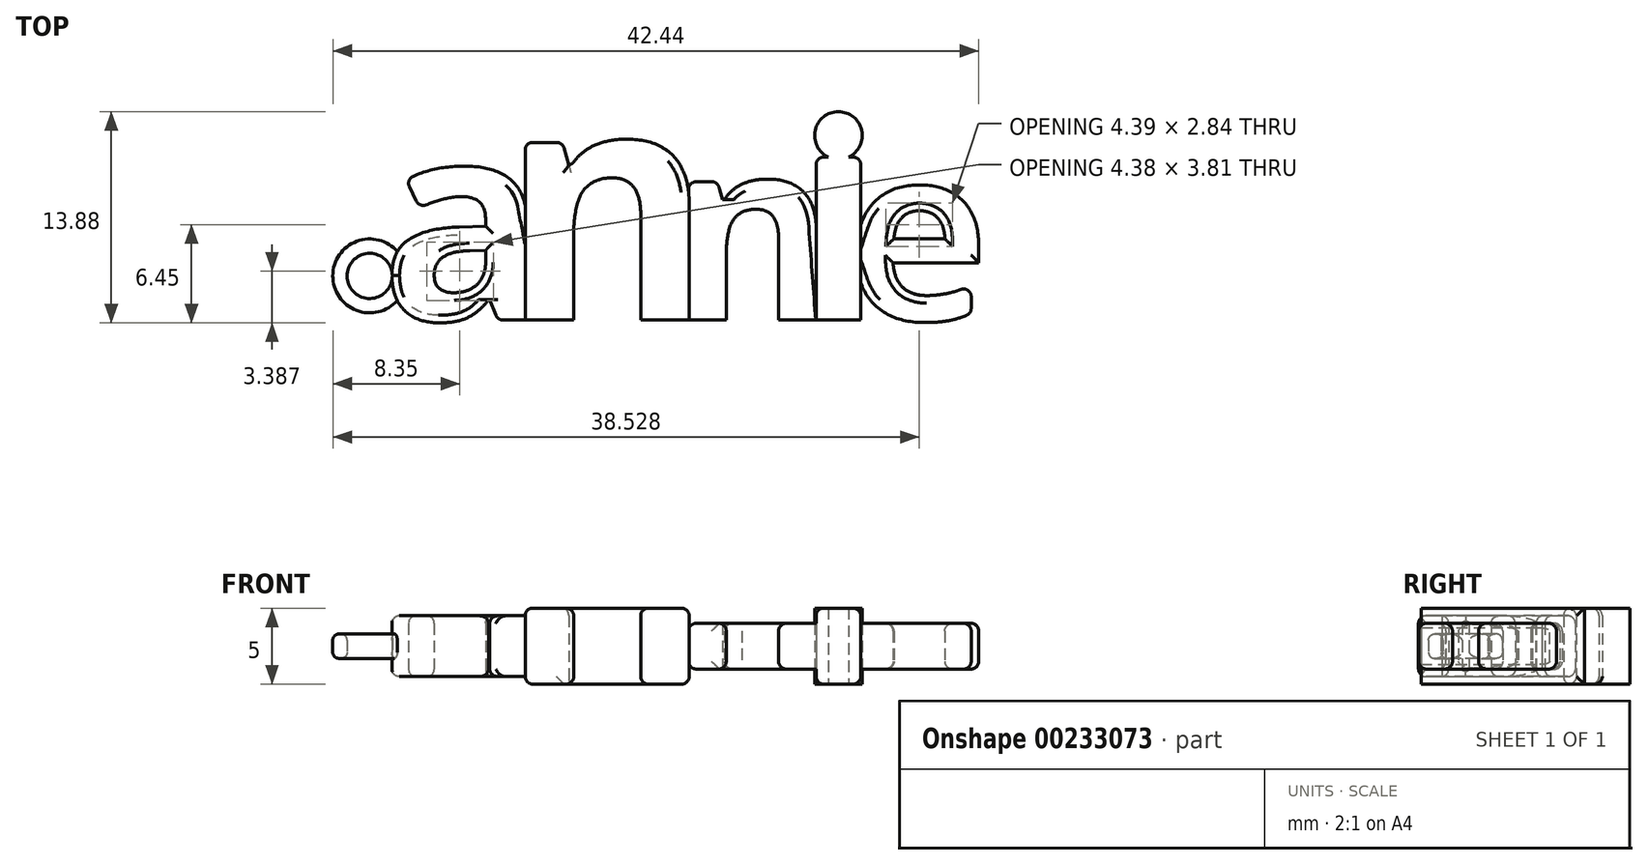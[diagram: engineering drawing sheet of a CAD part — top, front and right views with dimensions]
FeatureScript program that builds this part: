
annotation { "Feature Type Name" : "Feature", "Feature Type Description" : "" }
export const myFeature = defineFeature(function(context is Context, id is Id, definition is map)
    precondition{}
    {
        {
            var Q0;
            Q0=qCreatedBy(makeId("Top.planeOp"),FACE);
            var sketch = newSketch(context, id + "F0", { "sketchPlane" : qUnion([Q0])});
            skText(sketch, "E0", { "text": "a", "fontName": "OpenSans-Bold.ttf"});
            skText(sketch, "E1", { "text": "n", "fontName": "OpenSans-Bold.ttf"});
            skText(sketch, "E2", { "text": "n", "fontName": "OpenSans-Bold.ttf"});
            skText(sketch, "E3", { "text": "e", "fontName": "OpenSans-Bold.ttf"});
            skLineSegment(sketch, "E4.bottom", {"start": v(4.28, 10.72) * mm, "end": v(7.22, 10.72) * mm});
            skLineSegment(sketch, "E4.top", {"start": v(4.28, 0) * mm, "end": v(7.22, 0) * mm});
            skLineSegment(sketch, "E4.left", {"start": v(4.28, 10.72) * mm, "end": v(4.28, 0) * mm});
            skLineSegment(sketch, "E4.right", {"start": v(7.22, 10.72) * mm, "end": v(7.22, 0) * mm});
            skCircle(sketch, "E5", {"center": v(-25.05, 2.9) * mm, "radius": 2.43 * mm});
            skCircle(sketch, "E6", {"center": v(-25.05, 2.9) * mm, "radius": 1.48 * mm});
            skCircle(sketch, "E7", {"center": v(5.75, 12.13) * mm, "radius": 1.57 * mm});
            skPoint(sketch, "E7.centerSnap0", {"position": v(5.75, 10.72) * mm});
            const initialGuessF0  = {"E0": [-0.02435, 0, 1, 0, 0.01308], "E1": [-0.0165, 0, 1, 0, 0.0154], "E2": [-0.0054, 0, 1, 0, 0.012], "E3": [0.00622, 0, 1, 0, 0.0115]};
            skSetInitialGuess(sketch, initialGuessF0);
            skSolve(sketch);
        }
        {
            var Q0;
            {var subQ0=sQuery(id+"F0.wireOp",EDGE,"E5");var subQ1=sQuery(id+"F0.wireOp",EDGE,"E0.sketch_text.stroke-5");var subQ2=makeQuery(id+"F0.imprint","INTERSECT",VERTEX,{"derivedFrom":[subQ1,subQ0]});Q0=makeQuery(id+"F0.imprint","IMPRINT",FACE,{"disambiguationData":[TD([[makeQuery(id+"F0.imprint","IMPRINT",EDGE,{"disambiguationData":[TD([[subQ2,-1.0]])],"derivedFrom":subQ1}),-1.0]])]});}
            var Q1;
            Q1=makeQuery(id+"F0.imprint","IMPRINT",FACE,{"disambiguationData":[TD([[makeQuery(id+"F0.imprint","IMPRINT",EDGE,{"derivedFrom":sQuery(id+"F0.wireOp",EDGE,"E0.sketch_text.stroke-0")}),-1.0]])]});
            extrude(context, id + "F1", {"entities" : qUnion([Q0, Q1]), "depth" : 2 * mm, "hasSecondDirection" : true, "secondDirectionOppositeDirection" : true, "secondDirectionDepth" : 2 * mm});
        }
        {
            var Q0;
            {var subQ2=sQuery(id+"F0.wireOp",EDGE,"E1.sketch_text.stroke-16");Q0=makeQuery(id+"F0.imprint","IMPRINT",FACE,{"disambiguationData":[TD([[makeQuery(id+"F0.imprint","IMPRINT",EDGE,{"derivedFrom":subQ2}),1.0]])]});}
            extrude(context, id + "F2", {"entities" : qUnion([Q0]), "operationType" : NewBodyOperationType.ADD, "depth" : 1.5 * mm, "hasSecondDirection" : true, "secondDirectionOppositeDirection" : true, "secondDirectionDepth" : 1.5 * mm});
        }
        {
            var Q0;
            {var subQ1=sQuery(id+"F0.wireOp",EDGE,"E0.sketch_text.stroke-16");Q0=makeQuery(id+"F0.imprint","IMPRINT",FACE,{"disambiguationData":[TD([[makeQuery(id+"F0.imprint","IMPRINT",EDGE,{"derivedFrom":subQ1}),1.0]])]});}
            var Q1;
            {var subQ0=sQuery(id+"F0.wireOp",EDGE,"E0.sketch_text.stroke-16");Q1=makeQuery(id+"F0.imprint","IMPRINT",FACE,{"disambiguationData":[TD([[makeQuery(id+"F0.imprint","IMPRINT",EDGE,{"derivedFrom":subQ0}),-1.0]])]});}
            var Q2;
            {var subQ0=sQuery(id+"F0.wireOp",EDGE,"E1.sketch_text.stroke-16");Q2=makeQuery(id+"F0.imprint","IMPRINT",FACE,{"disambiguationData":[TD([[makeQuery(id+"F0.imprint","IMPRINT",EDGE,{"derivedFrom":subQ0}),-1.0]])]});}
            extrude(context, id + "F3", {"entities" : qUnion([Q0, Q1, Q2]), "depth" : 2.5 * mm, "hasSecondDirection" : true, "secondDirectionOppositeDirection" : true, "secondDirectionDepth" : 2.5 * mm});
        }
        {
            var Q0;
            {var subQ6=sQuery(id+"F0.wireOp",EDGE,"E2.sketch_text.stroke-16");Q0=makeQuery(id+"F0.imprint","IMPRINT",FACE,{"disambiguationData":[TD([[makeQuery(id+"F0.imprint","IMPRINT",EDGE,{"derivedFrom":subQ6}),1.0]])]});}
            var Q1;
            {var subQ0=sQuery(id+"F0.wireOp",EDGE,"E3.sketch_text.stroke-7");var subQ1=sQuery(id+"F0.wireOp",EDGE,"E3.sketch_text.stroke-6");var subQ2=makeQuery(id+"F0.imprint","INTERSECT",VERTEX,{"derivedFrom":[subQ1,subQ0]});Q1=makeQuery(id+"F0.imprint","IMPRINT",FACE,{"disambiguationData":[TD([[makeQuery(id+"F0.imprint","IMPRINT",EDGE,{"disambiguationData":[TD([[subQ2,1.0]])],"derivedFrom":subQ1}),-1.0]])]});}
            var Q2;
            {var subQ0=sQuery(id+"F0.wireOp",EDGE,"E7");var subQ1=sQuery(id+"F0.wireOp",EDGE,"E4.bottom");var subQ2=makeQuery(id+"F0.imprint","INTERSECT",VERTEX,{"disambiguationData":[OD(0.0)],"derivedFrom":[subQ1,subQ0]});Q2=makeQuery(id+"F0.imprint","IMPRINT",FACE,{"disambiguationData":[TD([[makeQuery(id+"F0.imprint","IMPRINT",EDGE,{"disambiguationData":[TD([[subQ2,-1.0]])],"derivedFrom":subQ1}),-1.0]])]});}
            var Q3;
            {var subQ0=sQuery(id+"F0.wireOp",EDGE,"E2.sketch_text.stroke-16");Q3=makeQuery(id+"F0.imprint","IMPRINT",FACE,{"disambiguationData":[TD([[makeQuery(id+"F0.imprint","IMPRINT",EDGE,{"derivedFrom":subQ0}),-1.0]])]});}
            var Q4;
            {var subQ0=sQuery(id+"F0.wireOp",EDGE,"E7");var subQ1=sQuery(id+"F0.wireOp",EDGE,"E4.bottom");var subQ2=makeQuery(id+"F0.imprint","INTERSECT",VERTEX,{"disambiguationData":[OD(0.0)],"derivedFrom":[subQ1,subQ0]});Q4=makeQuery(id+"F0.imprint","IMPRINT",FACE,{"disambiguationData":[TD([[makeQuery(id+"F0.imprint","IMPRINT",EDGE,{"disambiguationData":[TD([[subQ2,-1.0]])],"derivedFrom":subQ1}),1.0]])]});}
            extrude(context, id + "F4", {"entities" : qUnion([Q0, Q1, Q2, Q3, Q4]), "operationType" : NewBodyOperationType.ADD, "depth" : 2.5 * mm, "hasSecondDirection" : true, "secondDirectionOppositeDirection" : true, "secondDirectionDepth" : 2.5 * mm});
        }
        {
            var Q0;
            Q0=makeQuery(id+"F0.imprint","IMPRINT",FACE,{"disambiguationData":[TD([[makeQuery(id+"F0.imprint","IMPRINT",EDGE,{"derivedFrom":sQuery(id+"F0.wireOp",EDGE,"E3.sketch_text.stroke-0")}),-1.0]])]});
            extrude(context, id + "F5", {"entities" : qUnion([Q0]), "operationType" : NewBodyOperationType.ADD, "depth" : 1.5 * mm, "hasSecondDirection" : true, "secondDirectionOppositeDirection" : true, "secondDirectionDepth" : 1.5 * mm});
        }
        {
            var Q0;
            {var subQ0=sQuery(id+"F0.wireOp",EDGE,"E5");var subQ1=sQuery(id+"F0.wireOp",EDGE,"E0.sketch_text.stroke-5");var subQ2=makeQuery(id+"F0.imprint","INTERSECT",VERTEX,{"derivedFrom":[subQ1,subQ0]});Q0=makeQuery(id+"F0.imprint","IMPRINT",FACE,{"disambiguationData":[TD([[makeQuery(id+"F0.imprint","IMPRINT",EDGE,{"disambiguationData":[TD([[subQ2,-1.0]])],"derivedFrom":subQ1}),1.0]])]});}
            extrude(context, id + "F6", {"entities" : qUnion([Q0]), "depth" : 0.8 * mm, "hasSecondDirection" : true, "secondDirectionOppositeDirection" : true, "secondDirectionDepth" : 0.8 * mm});
        }
        {
            var Q0;
            Q0=makeQuery(id+"F6.opExtrude","CAP_EDGE",EDGE,{"disambiguationData":[OSD([sQuery(id+"F0.wireOp",EDGE,"E5")])],"isStart":false});
            var Q1;
            Q1=makeQuery(id+"F6.opExtrude","CAP_EDGE",EDGE,{"disambiguationData":[OSD([sQuery(id+"F0.wireOp",EDGE,"E5")])],"isStart":true});
            var Q2;
            Q2=makeQuery(id+"F6.opExtrude","CAP_EDGE",EDGE,{"disambiguationData":[OSD([sQuery(id+"F0.wireOp",EDGE,"E6")])],"isStart":false});
            var Q3;
            Q3=makeQuery(id+"F6.opExtrude","CAP_EDGE",EDGE,{"disambiguationData":[OSD([sQuery(id+"F0.wireOp",EDGE,"E6")])],"isStart":true});
            fillet(context, id + "F7", {"entities" : qUnion([Q0, Q1, Q2, Q3]), "radius" : 0.4 * mm, "tangentPropagation" : true, "allowEdgeOverflow" : false});
        }
        {
            var Q0;
            {var subQ0=sQuery(id+"F0.wireOp",EDGE,"E0.sketch_text.stroke-2");var subQ1=sQuery(id+"F0.wireOp",EDGE,"E0.sketch_text.stroke-1");Q0=makeQuery(id+"F1.boolean.opBoolean","MERGE",EDGE,{"derivedFrom":[makeQuery(id+"FrYbtXQuBTiY2Ud_0.opExtrude","SWEPT_EDGE",EDGE,{"disambiguationData":[OSD([subQ1,subQ0])]}),makeQuery(id+"F1.opExtrude","SWEPT_EDGE",EDGE,{"disambiguationData":[OSD([subQ1,subQ0])]})]});}
            var Q1;
            {var subQ0=sQuery(id+"F0.wireOp",EDGE,"E0.sketch_text.stroke-1");var subQ1=sQuery(id+"F0.wireOp",EDGE,"E0.sketch_text.stroke-0");Q1=makeQuery(id+"F1.boolean.opBoolean","MERGE",EDGE,{"derivedFrom":[makeQuery(id+"FrYbtXQuBTiY2Ud_0.opExtrude","SWEPT_EDGE",EDGE,{"disambiguationData":[OSD([subQ1,subQ0])]}),makeQuery(id+"F1.opExtrude","SWEPT_EDGE",EDGE,{"disambiguationData":[OSD([subQ1,subQ0])]})]});}
            var Q2;
            {var subQ0=sQuery(id+"F0.wireOp",EDGE,"E1.sketch_text.stroke-12");var subQ1=sQuery(id+"F0.wireOp",EDGE,"E1.sketch_text.stroke-11");Q2=makeQuery(id+"F3.boolean.opBoolean","MERGE",EDGE,{"derivedFrom":[makeQuery(id+"FrYbtXQuBTiY2Ud_0.opExtrude","SWEPT_EDGE",EDGE,{"disambiguationData":[OSD([subQ1,subQ0])]}),makeQuery(id+"F3.opExtrude","SWEPT_EDGE",EDGE,{"disambiguationData":[OSD([subQ1,subQ0])]})]});}
            var Q3;
            {var subQ0=sQuery(id+"F0.wireOp",EDGE,"E2.sketch_text.stroke-11");var subQ1=sQuery(id+"F0.wireOp",EDGE,"E2.sketch_text.stroke-10");Q3=makeQuery(id+"F2.boolean.opBoolean","MERGE",EDGE,{"derivedFrom":[makeQuery(id+"FrYbtXQuBTiY2Ud_0.opExtrude","SWEPT_EDGE",EDGE,{"disambiguationData":[OSD([subQ1,subQ0])]}),makeQuery(id+"F2.opExtrude","SWEPT_EDGE",EDGE,{"disambiguationData":[OSD([subQ1,subQ0])]})]});}
            var Q4;
            {var subQ0=sQuery(id+"F0.wireOp",EDGE,"E2.sketch_text.stroke-12");var subQ1=sQuery(id+"F0.wireOp",EDGE,"E2.sketch_text.stroke-11");Q4=makeQuery(id+"F2.boolean.opBoolean","MERGE",EDGE,{"derivedFrom":[makeQuery(id+"FrYbtXQuBTiY2Ud_0.opExtrude","SWEPT_EDGE",EDGE,{"disambiguationData":[OSD([subQ1,subQ0])]}),makeQuery(id+"F2.opExtrude","SWEPT_EDGE",EDGE,{"disambiguationData":[OSD([subQ1,subQ0])]})]});}
            fillet(context, id + "F8", {"entities" : qUnion([Q0, Q1, Q2, Q3, Q4]), "radius" : .6 * mm, "tangentPropagation" : true, "allowEdgeOverflow" : false});
        }
        {
            var Q0;
            Q0=makeQuery(id+"F1.opExtrude","CAP_EDGE",EDGE,{"disambiguationData":[OSD([sQuery(id+"F0.wireOp",EDGE,"E0.sketch_text.stroke-14")])],"isStart":false});
            var Q1;
            Q1=makeQuery(id+"F1.opExtrude","CAP_EDGE",EDGE,{"disambiguationData":[OSD([sQuery(id+"F0.wireOp",EDGE,"E0.sketch_text.stroke-15")])],"isStart":false});
            var Q2;
            Q2=makeQuery(id+"F1.opExtrude","CAP_EDGE",EDGE,{"disambiguationData":[OSD([sQuery(id+"F0.wireOp",EDGE,"E0.sketch_text.stroke-0")])],"isStart":false});
            var Q3;
            {var subQ0=sQuery(id+"F0.wireOp",EDGE,"E0.sketch_text.stroke-17");var subQ1=sQuery(id+"F0.wireOp",EDGE,"E0.sketch_text.stroke-0");Q3=makeQuery(id+"F1.boolean.opBoolean","MERGE",EDGE,{"derivedFrom":[makeQuery(id+"FrYbtXQuBTiY2Ud_0.opExtrude","SWEPT_EDGE",EDGE,{"disambiguationData":[OSD([subQ1,subQ0])]}),makeQuery(id+"F1.opExtrude","SWEPT_EDGE",EDGE,{"disambiguationData":[OSD([subQ1,subQ0])]})]});}
            var Q4;
            Q4=makeQuery(id+"F1.opExtrude","CAP_EDGE",EDGE,{"disambiguationData":[OSD([sQuery(id+"F0.wireOp",EDGE,"E0.sketch_text.stroke-2")])],"isStart":false});
            var Q5;
            Q5=makeQuery(id+"F1.opExtrude","CAP_EDGE",EDGE,{"disambiguationData":[OSD([sQuery(id+"F0.wireOp",EDGE,"E0.sketch_text.stroke-8")])],"isStart":false});
            var Q6;
            Q6=makeQuery(id+"F1.opExtrude","CAP_EDGE",EDGE,{"disambiguationData":[OSD([sQuery(id+"F0.wireOp",EDGE,"E0.sketch_text.stroke-11")])],"isStart":false});
            var Q7;
            Q7=makeQuery(id+"F1.opExtrude","CAP_EDGE",EDGE,{"disambiguationData":[OSD([sQuery(id+"F0.wireOp",EDGE,"E0.sketch_text.stroke-12")])],"isStart":false});
            var Q8;
            {var subQ0=sQuery(id+"F0.wireOp",EDGE,"E0.sketch_text.stroke-13");var subQ1=sQuery(id+"F0.wireOp",EDGE,"E0.sketch_text.stroke-12");Q8=makeQuery(id+"F1.boolean.opBoolean","MERGE",EDGE,{"derivedFrom":[makeQuery(id+"FrYbtXQuBTiY2Ud_0.opExtrude","SWEPT_EDGE",EDGE,{"disambiguationData":[OSD([subQ1,subQ0])]}),makeQuery(id+"F1.opExtrude","SWEPT_EDGE",EDGE,{"disambiguationData":[OSD([subQ1,subQ0])]})]});}
            var Q9;
            {var subQ0=sQuery(id+"F0.wireOp",EDGE,"E0.sketch_text.stroke-12");var subQ1=sQuery(id+"F0.wireOp",EDGE,"E0.sketch_text.stroke-11");Q9=makeQuery(id+"F1.boolean.opBoolean","MERGE",EDGE,{"derivedFrom":[makeQuery(id+"FrYbtXQuBTiY2Ud_0.opExtrude","SWEPT_EDGE",EDGE,{"disambiguationData":[OSD([subQ1,subQ0])]}),makeQuery(id+"F1.opExtrude","SWEPT_EDGE",EDGE,{"disambiguationData":[OSD([subQ1,subQ0])]})]});}
            var Q10;
            Q10=makeQuery(id+"F1.opExtrude","CAP_EDGE",EDGE,{"disambiguationData":[OSD([sQuery(id+"F0.wireOp",EDGE,"E0.sketch_text.stroke-12")])],"isStart":true});
            var Q11;
            Q11=makeQuery(id+"F1.opExtrude","CAP_EDGE",EDGE,{"disambiguationData":[OSD([sQuery(id+"F0.wireOp",EDGE,"E0.sketch_text.stroke-7")])],"isStart":false});
            var Q12;
            Q12=makeQuery(id+"F1.opExtrude","CAP_EDGE",EDGE,{"disambiguationData":[OSD([sQuery(id+"F0.wireOp",EDGE,"E0.sketch_text.stroke-21")])],"isStart":false});
            var Q13;
            Q13=makeQuery(id+"F1.opExtrude","CAP_EDGE",EDGE,{"disambiguationData":[OSD([sQuery(id+"F0.wireOp",EDGE,"E0.sketch_text.stroke-22")])],"isStart":false});
            var Q14;
            Q14=makeQuery(id+"F1.opExtrude","CAP_EDGE",EDGE,{"disambiguationData":[OSD([sQuery(id+"F0.wireOp",EDGE,"E0.sketch_text.stroke-23")])],"isStart":false});
            var Q15;
            Q15=makeQuery(id+"F1.opExtrude","CAP_EDGE",EDGE,{"disambiguationData":[OSD([sQuery(id+"F0.wireOp",EDGE,"E0.sketch_text.stroke-24")])],"isStart":false});
            var Q16;
            Q16=makeQuery(id+"F1.opExtrude","CAP_EDGE",EDGE,{"disambiguationData":[OSD([sQuery(id+"F0.wireOp",EDGE,"E0.sketch_text.stroke-18")])],"isStart":false});
            var Q17;
            Q17=makeQuery(id+"F1.opExtrude","CAP_EDGE",EDGE,{"disambiguationData":[OSD([sQuery(id+"F0.wireOp",EDGE,"E0.sketch_text.stroke-0")])],"isStart":true});
            var Q18;
            Q18=makeQuery(id+"F1.opExtrude","CAP_EDGE",EDGE,{"disambiguationData":[OSD([sQuery(id+"F0.wireOp",EDGE,"E0.sketch_text.stroke-2")])],"isStart":true});
            var Q19;
            Q19=makeQuery(id+"F1.opExtrude","CAP_EDGE",EDGE,{"disambiguationData":[OSD([sQuery(id+"F0.wireOp",EDGE,"E0.sketch_text.stroke-18")])],"isStart":true});
            var Q20;
            Q20=makeQuery(id+"F1.opExtrude","CAP_EDGE",EDGE,{"disambiguationData":[OSD([sQuery(id+"F0.wireOp",EDGE,"E0.sketch_text.stroke-24")])],"isStart":true});
            var Q21;
            Q21=makeQuery(id+"F1.opExtrude","CAP_EDGE",EDGE,{"disambiguationData":[OSD([sQuery(id+"F0.wireOp",EDGE,"E0.sketch_text.stroke-23")])],"isStart":true});
            var Q22;
            Q22=makeQuery(id+"F1.opExtrude","CAP_EDGE",EDGE,{"disambiguationData":[OSD([sQuery(id+"F0.wireOp",EDGE,"E0.sketch_text.stroke-22")])],"isStart":true});
            var Q23;
            Q23=makeQuery(id+"F1.opExtrude","CAP_EDGE",EDGE,{"disambiguationData":[OSD([sQuery(id+"F0.wireOp",EDGE,"E0.sketch_text.stroke-21")])],"isStart":true});
            var Q24;
            Q24=makeQuery(id+"F1.opExtrude","CAP_EDGE",EDGE,{"disambiguationData":[OSD([sQuery(id+"F0.wireOp",EDGE,"E0.sketch_text.stroke-7")])],"isStart":true});
            var Q25;
            Q25=makeQuery(id+"F1.opExtrude","CAP_EDGE",EDGE,{"disambiguationData":[OSD([sQuery(id+"F0.wireOp",EDGE,"E0.sketch_text.stroke-8")])],"isStart":true});
            var Q26;
            Q26=makeQuery(id+"F1.opExtrude","CAP_EDGE",EDGE,{"disambiguationData":[OSD([sQuery(id+"F0.wireOp",EDGE,"E0.sketch_text.stroke-11")])],"isStart":true});
            var Q27;
            Q27=makeQuery(id+"F1.opExtrude","CAP_EDGE",EDGE,{"disambiguationData":[OSD([sQuery(id+"F0.wireOp",EDGE,"E0.sketch_text.stroke-14")])],"isStart":true});
            var Q28;
            Q28=makeQuery(id+"F1.opExtrude","CAP_EDGE",EDGE,{"disambiguationData":[OSD([sQuery(id+"F0.wireOp",EDGE,"E0.sketch_text.stroke-15")])],"isStart":true});
            fillet(context, id + "F9", {"entities" : qUnion([Q0, Q1, Q2, Q3, Q4, Q5, Q6, Q7, Q8, Q9, Q10, Q11, Q12, Q13, Q14, Q15, Q16, Q17, Q18, Q19, Q20, Q21, Q22, Q23, Q24, Q25, Q26, Q27, Q28]), "radius" : .5 * mm, "tangentPropagation" : true, "allowEdgeOverflow" : false});
        }
        {
            var Q0;
            Q0=makeQuery(id+"F3.opExtrude","CAP_EDGE",EDGE,{"disambiguationData":[OSD([sQuery(id+"F0.wireOp",EDGE,"E1.sketch_text.stroke-8")])],"isStart":false});
            var Q1;
            Q1=makeQuery(id+"F3.opExtrude","CAP_EDGE",EDGE,{"disambiguationData":[OSD([sQuery(id+"F0.wireOp",EDGE,"E1.sketch_text.stroke-6")])],"isStart":false});
            var Q2;
            Q2=makeQuery(id+"F3.opExtrude","CAP_EDGE",EDGE,{"disambiguationData":[OSD([sQuery(id+"F0.wireOp",EDGE,"E1.sketch_text.stroke-16")])],"isStart":false});
            var Q3;
            Q3=makeQuery(id+"F3.opExtrude","CAP_EDGE",EDGE,{"disambiguationData":[OSD([sQuery(id+"F0.wireOp",EDGE,"E1.sketch_text.stroke-10")])],"isStart":false});
            var Q4;
            Q4=makeQuery(id+"F3.opExtrude","CAP_EDGE",EDGE,{"disambiguationData":[OSD([sQuery(id+"F0.wireOp",EDGE,"E1.sketch_text.stroke-9")])],"isStart":false});
            var Q5;
            {var subQ0=sQuery(id+"F0.wireOp",EDGE,"E1.sketch_text.stroke-9");var subQ1=sQuery(id+"F0.wireOp",EDGE,"E1.sketch_text.stroke-8");Q5=makeQuery(id+"F3.boolean.opBoolean","MERGE",EDGE,{"derivedFrom":[makeQuery(id+"FrYbtXQuBTiY2Ud_0.opExtrude","SWEPT_EDGE",EDGE,{"disambiguationData":[OSD([subQ1,subQ0])]}),makeQuery(id+"F3.opExtrude","SWEPT_EDGE",EDGE,{"disambiguationData":[OSD([subQ1,subQ0])]})]});}
            var Q6;
            Q6=makeQuery(id+"F3.opExtrude","CAP_EDGE",EDGE,{"disambiguationData":[OSD([sQuery(id+"F0.wireOp",EDGE,"E1.sketch_text.stroke-9")])],"isStart":true});
            var Q7;
            {var subQ0=sQuery(id+"F0.wireOp",EDGE,"E1.sketch_text.stroke-10");var subQ1=sQuery(id+"F0.wireOp",EDGE,"E1.sketch_text.stroke-9");Q7=makeQuery(id+"F3.boolean.opBoolean","MERGE",EDGE,{"derivedFrom":[makeQuery(id+"FrYbtXQuBTiY2Ud_0.opExtrude","SWEPT_EDGE",EDGE,{"disambiguationData":[OSD([subQ1,subQ0])]}),makeQuery(id+"F3.opExtrude","SWEPT_EDGE",EDGE,{"disambiguationData":[OSD([subQ1,subQ0])]})]});}
            var Q8;
            Q8=makeQuery(id+"F3.opExtrude","CAP_EDGE",EDGE,{"disambiguationData":[OSD([sQuery(id+"F0.wireOp",EDGE,"E1.sketch_text.stroke-6")])],"isStart":true});
            var Q9;
            Q9=makeQuery(id+"F3.opExtrude","CAP_EDGE",EDGE,{"disambiguationData":[OSD([sQuery(id+"F0.wireOp",EDGE,"E1.sketch_text.stroke-8")])],"isStart":true});
            var Q10;
            Q10=makeQuery(id+"F3.opExtrude","CAP_EDGE",EDGE,{"disambiguationData":[OSD([sQuery(id+"F0.wireOp",EDGE,"E1.sketch_text.stroke-16")])],"isStart":true});
            var Q11;
            {var subQ0=sQuery(id+"F0.wireOp",EDGE,"E2.sketch_text.stroke-9");Q11=makeQuery(id+"F2.boolean.opBoolean","MERGE",FACE,{"derivedFrom":[makeQuery(id+"FrYbtXQuBTiY2Ud_0.opExtrude","SWEPT_FACE",FACE,{"disambiguationData":[OSD([subQ0])]}),makeQuery(id+"F2.opExtrude","SWEPT_FACE",FACE,{"disambiguationData":[OSD([subQ0])]})]});}
            var Q12;
            {var subQ0=sQuery(id+"F0.wireOp",EDGE,"E2.sketch_text.stroke-11");var subQ1=sQuery(id+"F0.wireOp",EDGE,"E2.sketch_text.stroke-10");Q12=makeQuery(id+"F8.opFillet","BLEND_EDGE",EDGE,{"blendedFrom":[makeQuery(id+"F2.boolean.opBoolean","MERGE",EDGE,{"derivedFrom":[makeQuery(id+"FrYbtXQuBTiY2Ud_0.opExtrude","SWEPT_EDGE",EDGE,{"disambiguationData":[OSD([subQ1,subQ0])]}),makeQuery(id+"F2.opExtrude","SWEPT_EDGE",EDGE,{"disambiguationData":[OSD([subQ1,subQ0])]})]}),makeQuery(id+"F2.opExtrude","CAP_FACE",FACE,{"disambiguationData":[OSD([sQuery(id+"F0.wireOp",EDGE,"E1.sketch_text.stroke-15"),sQuery(id+"F0.wireOp",EDGE,"E1.sketch_text.stroke-16"),sQuery(id+"F0.wireOp",EDGE,"E2.sketch_text.stroke-0"),sQuery(id+"F0.wireOp",EDGE,"E2.sketch_text.stroke-1"),sQuery(id+"F0.wireOp",EDGE,"E2.sketch_text.stroke-2"),sQuery(id+"F0.wireOp",EDGE,"E2.sketch_text.stroke-3"),sQuery(id+"F0.wireOp",EDGE,"E2.sketch_text.stroke-4"),sQuery(id+"F0.wireOp",EDGE,"E2.sketch_text.stroke-5"),sQuery(id+"F0.wireOp",EDGE,"E2.sketch_text.stroke-6"),sQuery(id+"F0.wireOp",EDGE,"E2.sketch_text.stroke-7"),sQuery(id+"F0.wireOp",EDGE,"E2.sketch_text.stroke-8"),sQuery(id+"F0.wireOp",EDGE,"E2.sketch_text.stroke-9"),subQ1,subQ0,sQuery(id+"F0.wireOp",EDGE,"E2.sketch_text.stroke-12"),sQuery(id+"F0.wireOp",EDGE,"E2.sketch_text.stroke-13"),sQuery(id+"F0.wireOp",EDGE,"E2.sketch_text.stroke-14"),sQuery(id+"F0.wireOp",EDGE,"E2.sketch_text.stroke-15"),sQuery(id+"F0.wireOp",EDGE,"E4.left")])],"isStart":false})],"blendedInto":[makeQuery(id+"F2.opExtrude","CAP_FACE",FACE,{"disambiguationData":[OSD([sQuery(id+"F0.wireOp",EDGE,"E1.sketch_text.stroke-15"),sQuery(id+"F0.wireOp",EDGE,"E1.sketch_text.stroke-16"),sQuery(id+"F0.wireOp",EDGE,"E2.sketch_text.stroke-0"),sQuery(id+"F0.wireOp",EDGE,"E2.sketch_text.stroke-1"),sQuery(id+"F0.wireOp",EDGE,"E2.sketch_text.stroke-2"),sQuery(id+"F0.wireOp",EDGE,"E2.sketch_text.stroke-3"),sQuery(id+"F0.wireOp",EDGE,"E2.sketch_text.stroke-4"),sQuery(id+"F0.wireOp",EDGE,"E2.sketch_text.stroke-5"),sQuery(id+"F0.wireOp",EDGE,"E2.sketch_text.stroke-6"),sQuery(id+"F0.wireOp",EDGE,"E2.sketch_text.stroke-7"),sQuery(id+"F0.wireOp",EDGE,"E2.sketch_text.stroke-8"),sQuery(id+"F0.wireOp",EDGE,"E2.sketch_text.stroke-9"),subQ1,subQ0,sQuery(id+"F0.wireOp",EDGE,"E2.sketch_text.stroke-12"),sQuery(id+"F0.wireOp",EDGE,"E2.sketch_text.stroke-13"),sQuery(id+"F0.wireOp",EDGE,"E2.sketch_text.stroke-14"),sQuery(id+"F0.wireOp",EDGE,"E2.sketch_text.stroke-15"),sQuery(id+"F0.wireOp",EDGE,"E4.left")])],"isStart":false})]});}
            var Q13;
            Q13=makeQuery(id+"F2.opExtrude","CAP_EDGE",EDGE,{"disambiguationData":[OSD([sQuery(id+"F0.wireOp",EDGE,"E2.sketch_text.stroke-12")])],"isStart":false});
            var Q14;
            Q14=makeQuery(id+"F2.opExtrude","CAP_EDGE",EDGE,{"disambiguationData":[OSD([sQuery(id+"F0.wireOp",EDGE,"E2.sketch_text.stroke-6")])],"isStart":false});
            var Q15;
            Q15=makeQuery(id+"F2.opExtrude","CAP_EDGE",EDGE,{"disambiguationData":[OSD([sQuery(id+"F0.wireOp",EDGE,"E2.sketch_text.stroke-8")])],"isStart":false});
            var Q16;
            {var subQ0=sQuery(id+"F0.wireOp",EDGE,"E2.sketch_text.stroke-11");var subQ1=sQuery(id+"F0.wireOp",EDGE,"E2.sketch_text.stroke-10");Q16=makeQuery(id+"F8.opFillet","BLEND_EDGE",EDGE,{"blendedFrom":[makeQuery(id+"F2.boolean.opBoolean","MERGE",EDGE,{"derivedFrom":[makeQuery(id+"FrYbtXQuBTiY2Ud_0.opExtrude","SWEPT_EDGE",EDGE,{"disambiguationData":[OSD([subQ1,subQ0])]}),makeQuery(id+"F2.opExtrude","SWEPT_EDGE",EDGE,{"disambiguationData":[OSD([subQ1,subQ0])]})]}),makeQuery(id+"F2.opExtrude","CAP_FACE",FACE,{"disambiguationData":[OSD([sQuery(id+"F0.wireOp",EDGE,"E1.sketch_text.stroke-15"),sQuery(id+"F0.wireOp",EDGE,"E1.sketch_text.stroke-16"),sQuery(id+"F0.wireOp",EDGE,"E2.sketch_text.stroke-0"),sQuery(id+"F0.wireOp",EDGE,"E2.sketch_text.stroke-1"),sQuery(id+"F0.wireOp",EDGE,"E2.sketch_text.stroke-2"),sQuery(id+"F0.wireOp",EDGE,"E2.sketch_text.stroke-3"),sQuery(id+"F0.wireOp",EDGE,"E2.sketch_text.stroke-4"),sQuery(id+"F0.wireOp",EDGE,"E2.sketch_text.stroke-5"),sQuery(id+"F0.wireOp",EDGE,"E2.sketch_text.stroke-6"),sQuery(id+"F0.wireOp",EDGE,"E2.sketch_text.stroke-7"),sQuery(id+"F0.wireOp",EDGE,"E2.sketch_text.stroke-8"),sQuery(id+"F0.wireOp",EDGE,"E2.sketch_text.stroke-9"),subQ1,subQ0,sQuery(id+"F0.wireOp",EDGE,"E2.sketch_text.stroke-12"),sQuery(id+"F0.wireOp",EDGE,"E2.sketch_text.stroke-13"),sQuery(id+"F0.wireOp",EDGE,"E2.sketch_text.stroke-14"),sQuery(id+"F0.wireOp",EDGE,"E2.sketch_text.stroke-15"),sQuery(id+"F0.wireOp",EDGE,"E4.left")])],"isStart":true})],"blendedInto":[makeQuery(id+"F2.opExtrude","CAP_FACE",FACE,{"disambiguationData":[OSD([sQuery(id+"F0.wireOp",EDGE,"E1.sketch_text.stroke-15"),sQuery(id+"F0.wireOp",EDGE,"E1.sketch_text.stroke-16"),sQuery(id+"F0.wireOp",EDGE,"E2.sketch_text.stroke-0"),sQuery(id+"F0.wireOp",EDGE,"E2.sketch_text.stroke-1"),sQuery(id+"F0.wireOp",EDGE,"E2.sketch_text.stroke-2"),sQuery(id+"F0.wireOp",EDGE,"E2.sketch_text.stroke-3"),sQuery(id+"F0.wireOp",EDGE,"E2.sketch_text.stroke-4"),sQuery(id+"F0.wireOp",EDGE,"E2.sketch_text.stroke-5"),sQuery(id+"F0.wireOp",EDGE,"E2.sketch_text.stroke-6"),sQuery(id+"F0.wireOp",EDGE,"E2.sketch_text.stroke-7"),sQuery(id+"F0.wireOp",EDGE,"E2.sketch_text.stroke-8"),sQuery(id+"F0.wireOp",EDGE,"E2.sketch_text.stroke-9"),subQ1,subQ0,sQuery(id+"F0.wireOp",EDGE,"E2.sketch_text.stroke-12"),sQuery(id+"F0.wireOp",EDGE,"E2.sketch_text.stroke-13"),sQuery(id+"F0.wireOp",EDGE,"E2.sketch_text.stroke-14"),sQuery(id+"F0.wireOp",EDGE,"E2.sketch_text.stroke-15"),sQuery(id+"F0.wireOp",EDGE,"E4.left")])],"isStart":true})]});}
            var Q17;
            Q17=makeQuery(id+"F2.opExtrude","CAP_EDGE",EDGE,{"disambiguationData":[OSD([sQuery(id+"F0.wireOp",EDGE,"E2.sketch_text.stroke-12")])],"isStart":true});
            var Q18;
            Q18=makeQuery(id+"F2.opExtrude","CAP_EDGE",EDGE,{"disambiguationData":[OSD([sQuery(id+"F0.wireOp",EDGE,"E2.sketch_text.stroke-8")])],"isStart":true});
            var Q19;
            Q19=makeQuery(id+"F2.opExtrude","CAP_EDGE",EDGE,{"disambiguationData":[OSD([sQuery(id+"F0.wireOp",EDGE,"E2.sketch_text.stroke-6")])],"isStart":true});
            fillet(context, id + "F10", {"entities" : qUnion([Q0, Q1, Q2, Q3, Q4, Q5, Q6, Q7, Q8, Q9, Q10, Q11, Q12, Q13, Q14, Q15, Q16, Q17, Q18, Q19]), "radius" : .5 * mm, "tangentPropagation" : true, "allowEdgeOverflow" : false});
        }
        {
            var Q0;
            Q0=makeQuery(id+"F4.opExtrude","CAP_EDGE",EDGE,{"disambiguationData":[OSD([sQuery(id+"F0.wireOp",EDGE,"E4.left")])],"isStart":false});
            var Q1;
            Q1=makeQuery(id+"F4.opExtrude","CAP_EDGE",EDGE,{"disambiguationData":[OSD([sQuery(id+"F0.wireOp",EDGE,"E4.right")])],"isStart":false});
            var Q2;
            Q2=makeQuery(id+"F4.opExtrude","CAP_EDGE",EDGE,{"disambiguationData":[OSD([sQuery(id+"F0.wireOp",EDGE,"E4.left")])],"isStart":true});
            var Q3;
            {var subQ0=sQuery(id+"F0.wireOp",EDGE,"E4.right");var subQ1=sQuery(id+"F0.wireOp",EDGE,"E4.bottom");Q3=makeQuery(id+"F4.boolean.opBoolean","MERGE",EDGE,{"derivedFrom":[makeQuery(id+"FrYbtXQuBTiY2Ud_0.opExtrude","SWEPT_EDGE",EDGE,{"disambiguationData":[OSD([subQ1,subQ0])]}),makeQuery(id+"F4.opExtrude","SWEPT_EDGE",EDGE,{"disambiguationData":[OSD([subQ1,subQ0])]})]});}
            var Q4;
            Q4=makeQuery(id+"F4.opExtrude","CAP_EDGE",EDGE,{"disambiguationData":[OSD([sQuery(id+"F0.wireOp",EDGE,"E4.right")])],"isStart":true});
            var Q5;
            {var subQ0=sQuery(id+"F0.wireOp",EDGE,"E4.left");var subQ1=sQuery(id+"F0.wireOp",EDGE,"E4.bottom");Q5=makeQuery(id+"F4.boolean.opBoolean","MERGE",EDGE,{"derivedFrom":[makeQuery(id+"FrYbtXQuBTiY2Ud_0.opExtrude","SWEPT_EDGE",EDGE,{"disambiguationData":[OSD([subQ1,subQ0])]}),makeQuery(id+"F4.opExtrude","SWEPT_EDGE",EDGE,{"disambiguationData":[OSD([subQ1,subQ0])]})]});}
            fillet(context, id + "F11", {"entities" : qUnion([Q0, Q1, Q2, Q3, Q4, Q5]), "radius" : .5 * mm, "tangentPropagation" : true, "allowEdgeOverflow" : false});
        }
        {
            var Q0;
            Q0=makeQuery(id+"F5.opExtrude","CAP_EDGE",EDGE,{"disambiguationData":[OSD([sQuery(id+"F0.wireOp",EDGE,"E3.sketch_text.stroke-9")])],"isStart":false});
            var Q1;
            Q1=makeQuery(id+"F5.opExtrude","CAP_EDGE",EDGE,{"disambiguationData":[OSD([sQuery(id+"F0.wireOp",EDGE,"E3.sketch_text.stroke-19")])],"isStart":false});
            var Q2;
            Q2=makeQuery(id+"F5.opExtrude","CAP_EDGE",EDGE,{"disambiguationData":[OSD([sQuery(id+"F0.wireOp",EDGE,"E3.sketch_text.stroke-17")])],"isStart":false});
            var Q3;
            Q3=makeQuery(id+"F5.opExtrude","CAP_EDGE",EDGE,{"disambiguationData":[OSD([sQuery(id+"F0.wireOp",EDGE,"E3.sketch_text.stroke-16")])],"isStart":false});
            var Q4;
            Q4=makeQuery(id+"F5.opExtrude","CAP_EDGE",EDGE,{"disambiguationData":[OSD([sQuery(id+"F0.wireOp",EDGE,"E3.sketch_text.stroke-12")])],"isStart":false});
            var Q5;
            Q5=makeQuery(id+"F5.opExtrude","CAP_EDGE",EDGE,{"disambiguationData":[OSD([sQuery(id+"F0.wireOp",EDGE,"E3.sketch_text.stroke-2")])],"isStart":false});
            var Q6;
            Q6=makeQuery(id+"F5.opExtrude","CAP_EDGE",EDGE,{"disambiguationData":[OSD([sQuery(id+"F0.wireOp",EDGE,"E3.sketch_text.stroke-3")])],"isStart":false});
            var Q7;
            {var subQ0=sQuery(id+"F0.wireOp",EDGE,"E3.sketch_text.stroke-18");var subQ1=sQuery(id+"F0.wireOp",EDGE,"E3.sketch_text.stroke-17");Q7=makeQuery(id+"F5.boolean.opBoolean","MERGE",EDGE,{"derivedFrom":[makeQuery(id+"FrYbtXQuBTiY2Ud_0.opExtrude","SWEPT_EDGE",EDGE,{"disambiguationData":[OSD([subQ1,subQ0])]}),makeQuery(id+"F5.opExtrude","SWEPT_EDGE",EDGE,{"disambiguationData":[OSD([subQ1,subQ0])]})]});}
            var Q8;
            {var subQ0=sQuery(id+"F0.wireOp",EDGE,"E3.sketch_text.stroke-17");var subQ1=sQuery(id+"F0.wireOp",EDGE,"E3.sketch_text.stroke-16");Q8=makeQuery(id+"F5.boolean.opBoolean","MERGE",EDGE,{"derivedFrom":[makeQuery(id+"FrYbtXQuBTiY2Ud_0.opExtrude","SWEPT_EDGE",EDGE,{"disambiguationData":[OSD([subQ1,subQ0])]}),makeQuery(id+"F5.opExtrude","SWEPT_EDGE",EDGE,{"disambiguationData":[OSD([subQ1,subQ0])]})]});}
            var Q9;
            Q9=makeQuery(id+"F5.opExtrude","CAP_EDGE",EDGE,{"disambiguationData":[OSD([sQuery(id+"F0.wireOp",EDGE,"E3.sketch_text.stroke-19")])],"isStart":true});
            var Q10;
            Q10=makeQuery(id+"F5.opExtrude","CAP_EDGE",EDGE,{"disambiguationData":[OSD([sQuery(id+"F0.wireOp",EDGE,"E3.sketch_text.stroke-16")])],"isStart":true});
            var Q11;
            Q11=makeQuery(id+"F5.opExtrude","CAP_EDGE",EDGE,{"disambiguationData":[OSD([sQuery(id+"F0.wireOp",EDGE,"E3.sketch_text.stroke-17")])],"isStart":true});
            var Q12;
            Q12=makeQuery(id+"F5.opExtrude","CAP_EDGE",EDGE,{"disambiguationData":[OSD([sQuery(id+"F0.wireOp",EDGE,"E3.sketch_text.stroke-12")])],"isStart":true});
            var Q13;
            Q13=makeQuery(id+"F5.opExtrude","CAP_EDGE",EDGE,{"disambiguationData":[OSD([sQuery(id+"F0.wireOp",EDGE,"E3.sketch_text.stroke-2")])],"isStart":true});
            var Q14;
            Q14=makeQuery(id+"F5.opExtrude","CAP_EDGE",EDGE,{"disambiguationData":[OSD([sQuery(id+"F0.wireOp",EDGE,"E3.sketch_text.stroke-3")])],"isStart":true});
            var Q15;
            Q15=makeQuery(id+"F5.opExtrude","CAP_EDGE",EDGE,{"disambiguationData":[OSD([sQuery(id+"F0.wireOp",EDGE,"E3.sketch_text.stroke-9")])],"isStart":true});
            fillet(context, id + "F12", {"entities" : qUnion([Q0, Q1, Q2, Q3, Q4, Q5, Q6, Q7, Q8, Q9, Q10, Q11, Q12, Q13, Q14, Q15]), "radius" : .5 * mm, "tangentPropagation" : true, "allowEdgeOverflow" : false});
        }
    });
